# Revit family: UVPPHD
name_source: partatom
category: Communication Devices
units: mm (PartAtom-declared; Revit-internal decimal feet)

## family parameters
Cut with Voids When Loaded = No
Host = Face
Maintain Annotation Orientation = No
OmniClass Number = 23.85.80.11.27
OmniClass Title = Lighting Controls
Part Type = Normal
Room Calculation Point = No
Round Connector Dimension = Use Diameter
Shared = Yes

## types (1)
- UVPPHD
    Assembly Code = D5090
    Certification = UL and cUL Listed
    Default Elevation = 48 "
    Description = The Universal Voltage Power Pack (UVPPHD) is a self-contained transformer and mechanical latching relay designed for low-voltage 24VDC occupancy sensors.
The power pack supports and automatically detects the line-voltage input within the 100–277VAC range. This eliminates the need for voltage-specific power packs. The Universal Voltage Power Pack with optional Manual ON/OFF control provides a unique solution for lighting applications where users require both manual ON/OFF control as well as automatic OFF control.
    Features = Robust latching relay provides unsurpassed and unrestricted performance
• Universal voltage: 100–277VAC; 50/60Hz
• Automatic voltage detection
• Electrical load switching capability: maximum of 20 Amps
• Regulated 24VDC current; 250mA output 
• Zero Arc Point Switching
• Plenum rated
• Mounts: inside or outside a junction box; inside a fixture
• UL and cUL listed
• Five-year limited warranty
• Low voltage device: 24 VDC
• Auto or Manual “ON” operation
• Powers up to six low voltage sensors
    Housing Material = Paint - Carbon Black
    L = 5.3 "
    Manufacturer = NX Lighting Controls
    Model = Heavy Duty Universal Voltage Power Packs
    Type Comments = Power Packs and Relays
    URL = https://www.currentlighting.com
    Warranty = 5-Years Warranty
    Washer = Metal-Galvanized_Steel

## geometry (parser evidence)
native form markers: Sweep x2
no freeform markers — native parametric forms only
